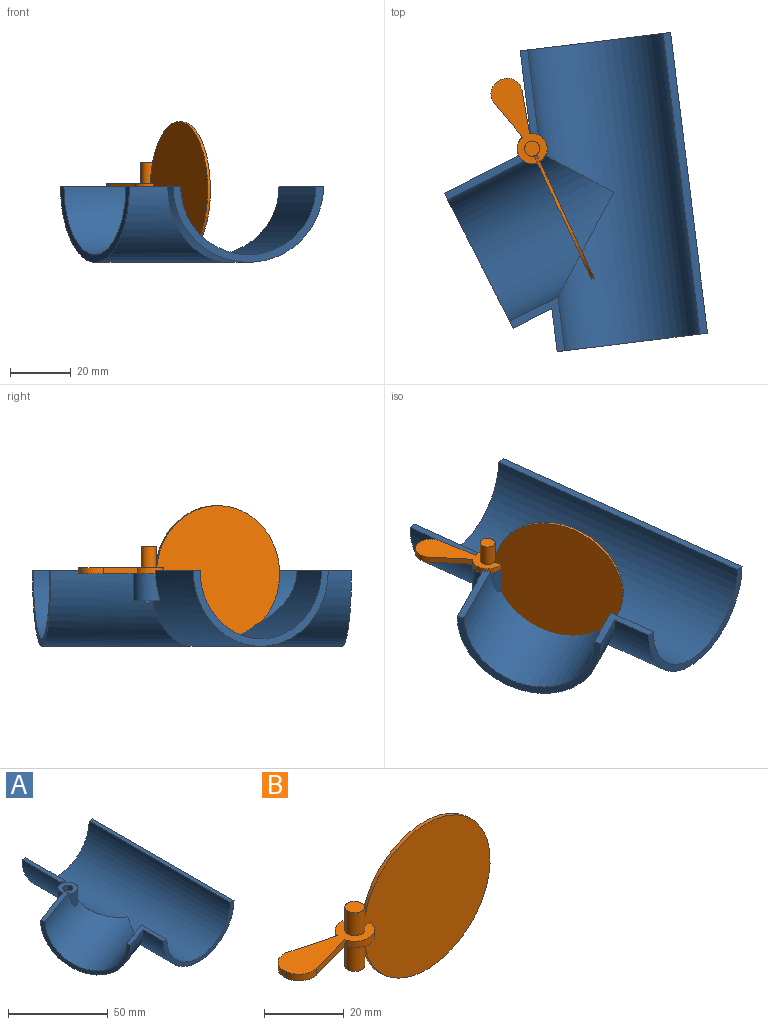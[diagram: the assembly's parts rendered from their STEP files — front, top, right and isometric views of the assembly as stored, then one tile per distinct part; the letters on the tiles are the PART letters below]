
ASSEMBLY  parts=2 mates=1
PART A: 21 faces, bbox 80.5x100x25 mm
  f0: plane 8.52x7.09mm, normal (0,0,-1), area 29.2mm2, adj f5,f7,f15,f20
  f1: plane 28.16x2.5mm, normal (0,0,1), area 69.3mm2, adj f7,f8,f11,f18
  f2: plane 17.87x16.79mm, normal (0,0,1), area 80.4mm2, adj f5,f6,f7,f9,f10,f11
  f3: plane 100x2.5mm, normal (0,0,1), area 250mm2, adj f7,f8,f9,f11
  f4: plane 27.32x11.75mm, normal (0,0,1), area 69.3mm2, adj f5,f6,f10,f17
  f5: cylinder r=25mm len=64.09mm, axis (-0.94,-0.34,0), area 2539.4mm2, adj f0,f2,f4,f6,f7,f15,f16,f17
  f6: plane 46.98x25mm, normal (-0.94,-0.34,0), area 186.5mm2, adj f2,f4,f5,f10
  f7: cylinder r=25mm len=100mm, axis (0,-1,0), area 6466.3mm2, adj f0,f1,f2,f3,f5,f8,f9,f15
  f8: plane 50x25mm, normal (0,1,0), area 186.5mm2, adj f1,f3,f7,f11
  f9: plane 50x25mm, normal (0,-1,0), area 186.5mm2, adj f2,f3,f7,f11
  f10: cylinder r=22.5mm len=62.38mm, axis (-0.94,-0.34,0), area 2397.1mm2, adj f2,f4,f6,f11,f13,f14,f17
  f11: cylinder r=22.5mm len=100mm, axis (0,-1,0), area 5931.4mm2, adj f1,f2,f3,f8,f9,f10,f12,f13
  f12: plane 2.48x0.16mm, normal (0,0,-1), area 0.3mm2, adj f11,f13
  f13: cylinder r=5mm len=9.32mm, axis (0,0,1), area 125.9mm2, adj f10,f11,f12,f14,f19
  f14: plane 2.33x0.85mm, normal (0,0,-1), area 0.3mm2, adj f10,f13
  f15: cylinder r=5mm len=9mm, axis (0,0,1), area 100.2mm2, adj f0,f5,f7,f19
  f16: plane 0.11x0.08mm, normal (0,0,-1), area 0mm2, adj f5,f7,f20
  f17: cylinder r=5mm len=2.14mm, axis (0,0,1), area 2.6mm2, adj f4,f5,f10,f19
  f18: cylinder r=5mm len=2.52mm, axis (0,0,1), area 2.6mm2, adj f1,f7,f11,f19
  f19: plane 10x10mm, normal (0,0,1), area 58.9mm2, adj f13,f15,f17,f18,f20
  f20: cylinder r=2.5mm len=9.9mm, axis (0,0,1), area 144.9mm2, adj f0,f5,f7,f16,f19
PART B: 16 faces, bbox 72.5x10.4x44.9 mm
  f0: cylinder r=22.45mm len=44.9mm, axis (0,1,0), area 139.1mm2, adj f1,f2,f7,f8
  f1: plane 44.9x44.9mm, normal (0,-1,0), area 1578.8mm2, adj f0,f7,f8,f13
  f2: plane 44.9x44.9mm, normal (0,1,0), area 1578.8mm2, adj f0,f3,f7,f8
  f3: cylinder r=4.95mm len=9.71mm, axis (0,0,-1), area 27.5mm2, adj f2,f4,f7,f8
  f4: plane 13.92x3.73mm, normal (0.26,0.97,0), area 28.8mm2, adj f3,f7,f8,f9
  f5: plane 13.92x3.73mm, normal (0.26,-0.97,0), area 28.8mm2, adj f7,f8,f10,f13
  f6: plane 2x0.37mm, normal (-1,0,0), area 0.7mm2, adj f7,f8,f9,f10
  f7: plane 29.93x10.37mm, normal (0,0,1), area 196.8mm2, adj f0,f1,f2,f3,f4,f5,f6,f9
  f8: plane 29.93x10.37mm, normal (0,0,-1), area 196.7mm2, adj f0,f1,f2,f3,f4,f5,f6,f9
  f9: cylinder r=5mm len=6.29mm, axis (0,0,-1), area 18.3mm2, adj f4,f6,f7,f8
  f10: cylinder r=5mm len=6.29mm, axis (0,0,-1), area 18.3mm2, adj f5,f6,f7,f8
  f11: cylinder r=2.5mm len=7mm, axis (0,0,-1), area 110mm2, adj f7,f12
  f12: plane 5x5mm, normal (0,0,1), area 19.6mm2, adj f11
  f13: cylinder r=4.95mm len=9.71mm, axis (0,0,-1), area 27.5mm2, adj f1,f5,f7,f8
  f14: plane 5x5mm, normal (0,0,-1), area 19.6mm2, adj f15
  f15: cylinder r=2.5mm len=9mm, axis (0,0,-1), area 141.4mm2, adj f8,f14
PLACE A rot(axis=(0,0,1),7deg) t=(55.76,86.06,0.11)mm
PLACE B rot(axis=(0,0,-1),65deg) t=(23.51,70.34,0.11)mm
MATE revolute B.f3 <-> A.f13  axis (0,0,-1) through (28.81,100.39,8.11)mm
